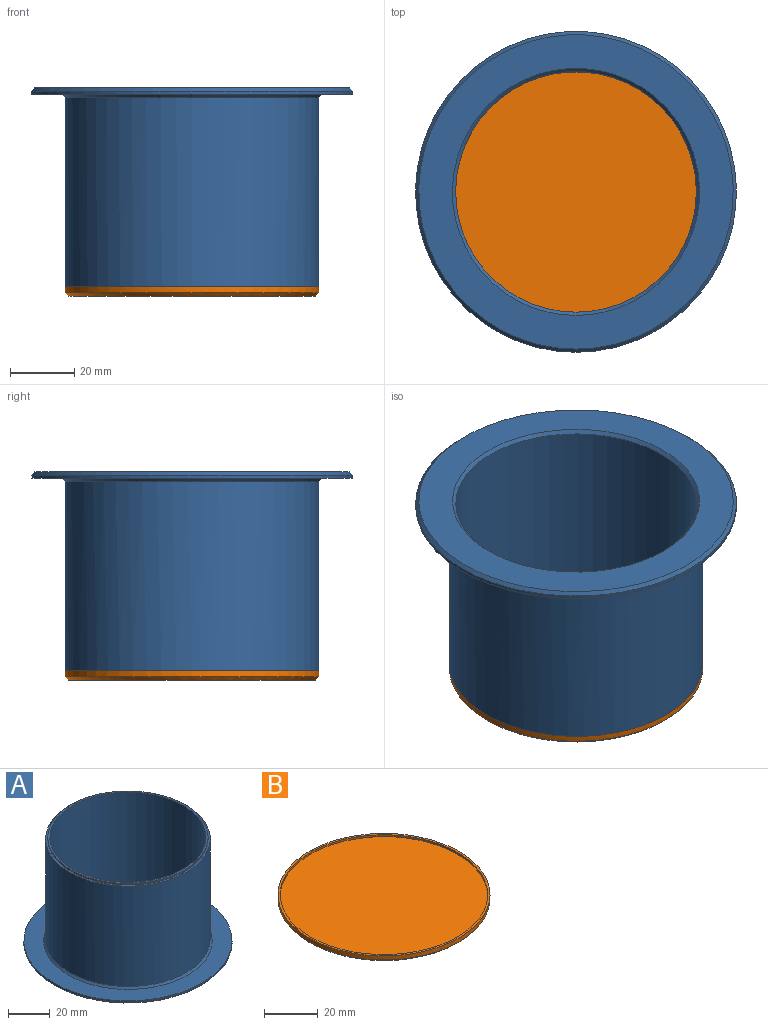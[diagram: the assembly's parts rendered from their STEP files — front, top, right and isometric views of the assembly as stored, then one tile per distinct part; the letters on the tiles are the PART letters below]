
ASSEMBLY  parts=2 mates=1
PART A: 11 faces, bbox 100x100x62.9 mm
  f0: cylinder r=37.5mm len=75mm, axis (0,0,-1), area 14573.1mm2, adj f8,f10
  f1: cylinder r=39.5mm len=79mm, axis (0,0,-1), area 14643mm2, adj f2,f6
  f2: plane 79x79mm, normal (0,0,1), area 245mm2, adj f1,f9
  f3: cylinder r=50mm len=100mm, axis (0,0,1), area 314.2mm2, adj f5,f7
  f4: plane 98x98mm, normal (0,0,-1), area 2886.3mm2, adj f7,f8
  f5: plane 100x100mm, normal (0,0,1), area 2701mm2, adj f3,f6
  f6: cone r=39.5mm half-angle=45deg, axis (0,0,-1), area 355.4mm2, adj f1,f5
  f7: cone r=49mm half-angle=45deg, axis (0,0,1), area 439.8mm2, adj f3,f4
  f8: cone r=38.5mm half-angle=45deg, axis (0,0,-1), area 337.7mm2, adj f0,f4
  f9: cylinder r=38.5mm len=77mm, axis (0,0,-1), area 205.6mm2, adj f2,f10
  f10: plane 77x77mm, normal (0,0,1), area 238.8mm2, adj f0,f9
PART B: 6 faces, bbox 79x79x2.9 mm
  f0: cylinder r=39.5mm len=79mm, axis (0,0,-1), area 459.1mm2, adj f3,f5
  f1: plane 77x77mm, normal (0,0,-1), area 4656.6mm2, adj f5
  f2: cylinder r=38.65mm len=77.3mm, axis (0,0,-1), area 206.4mm2, adj f3,f4
  f3: plane 79x79mm, normal (0,0,1), area 208.7mm2, adj f0,f2
  f4: plane 77.3x77.3mm, normal (0,0,1), area 4693mm2, adj f2
  f5: cone r=39.5mm half-angle=45deg, axis (0,0,1), area 346.5mm2, adj f0,f1
PLACE A rot(axis=(0.71,0.71,0),180deg) t=(-15.78,31.07,104.44)mm
PLACE B t=(-15.78,31.07,41.59)mm
MATE cylindrical A.f1 <-> B.f0  axis (0,0,-1) through (-15.78,31.07,43.59)mm
